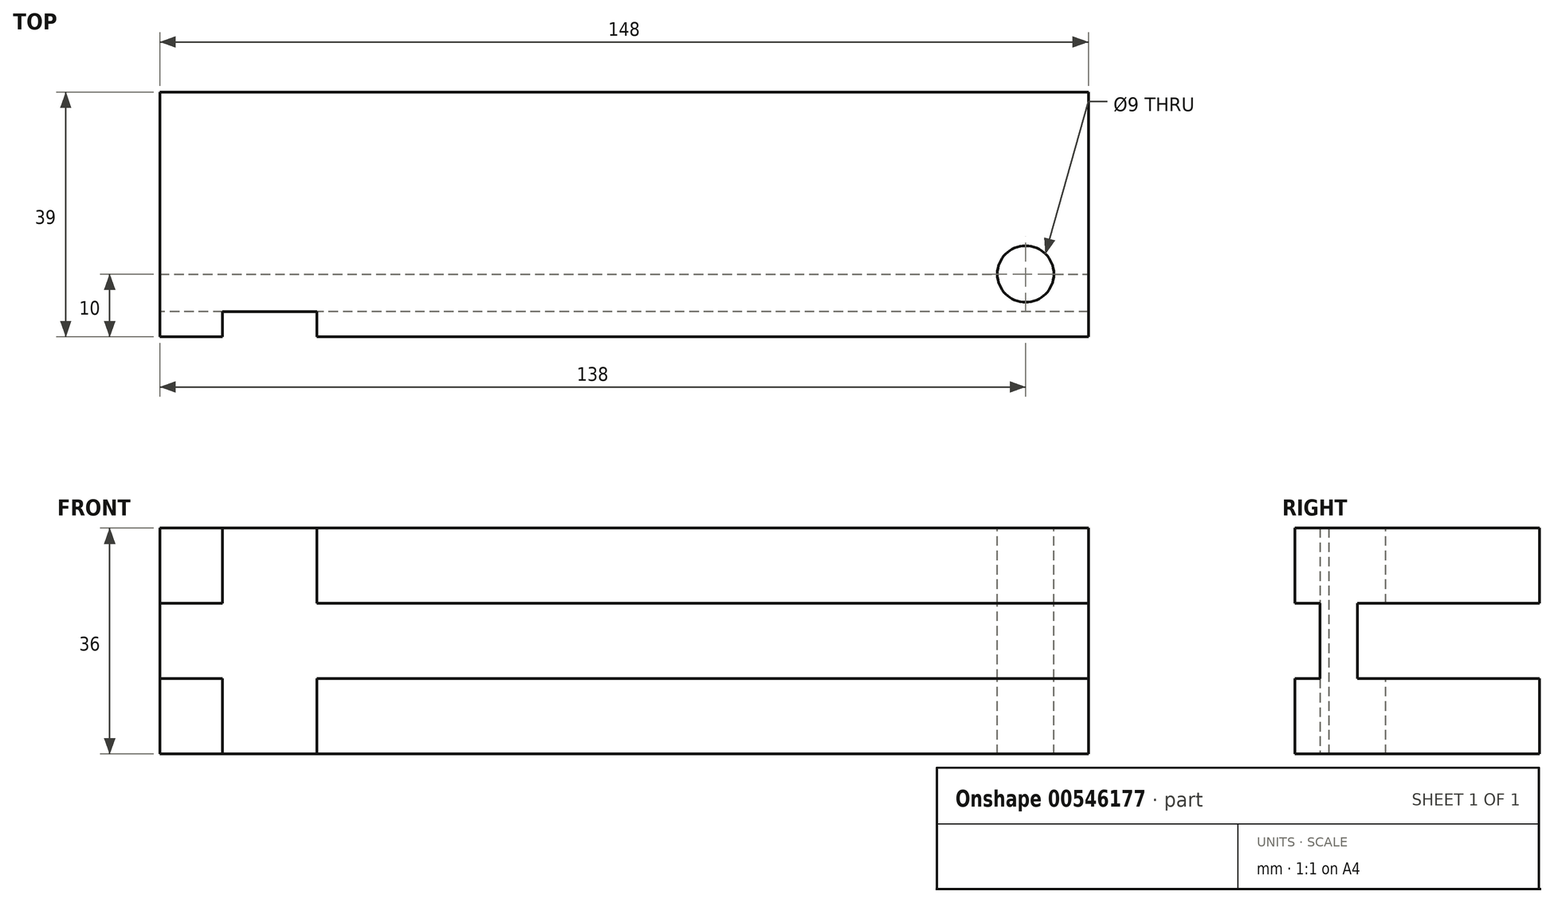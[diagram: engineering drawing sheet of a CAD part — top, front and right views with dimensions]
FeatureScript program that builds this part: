
annotation { "Feature Type Name" : "Feature", "Feature Type Description" : "" }
export const myFeature = defineFeature(function(context is Context, id is Id, definition is map)
    precondition{}
    {
        {
            var Q0;
            Q0=qCreatedBy(makeId("Front.planeOp"),FACE);
            var sketch = newSketch(context, id + "F0", { "sketchPlane" : qUnion([Q0])});
            skLineSegment(sketch, "E0.bottom", {"start": v(-74, 18) * mm, "end": v(74, 18) * mm});
            skLineSegment(sketch, "E0.top", {"start": v(-74, -18) * mm, "end": v(74, -18) * mm});
            skLineSegment(sketch, "E0.left", {"start": v(-74, 18) * mm, "end": v(-74, -18) * mm});
            skLineSegment(sketch, "E0.right", {"start": v(74, 18) * mm, "end": v(74, -18) * mm});
            skPoint(sketch, "E0.middle", {"position": v(0, 0) * mm});
            skLineSegment(sketch, "E1.bottom", {"start": v(-74, 6) * mm, "end": v(74, 6) * mm});
            skLineSegment(sketch, "E1.top", {"start": v(-74, -6) * mm, "end": v(74, -6) * mm});
            skLineSegment(sketch, "E1.left", {"start": v(-74, 6) * mm, "end": v(-74, -6) * mm});
            skLineSegment(sketch, "E1.right", {"start": v(74, 6) * mm, "end": v(74, -6) * mm});
            skSolve(sketch);
        }
        {
            var Q0;
            Q0=makeQuery(id+"F0.imprint","IMPRINT",FACE,{"disambiguationData":[TD([[makeQuery(id+"F0.imprint","IMPRINT",EDGE,{"derivedFrom":sQuery(id+"F0.wireOp",EDGE,"E0.bottom")}),-1.0]])]});
            var Q1;
            {var subQ0=sQuery(id+"F0.wireOp",EDGE,"E0.top");Q1=makeQuery(id+"F0.imprint","IMPRINT",FACE,{"disambiguationData":[TD([[makeQuery(id+"F0.imprint","IMPRINT",EDGE,{"derivedFrom":subQ0}),1.0]])]});}
            var Q2;
            Q2=makeQuery(id+"F0.imprint","IMPRINT",FACE,{"disambiguationData":[TD([[makeQuery(id+"F0.imprint","IMPRINT",EDGE,{"derivedFrom":sQuery(id+"F0.wireOp",EDGE,"E1.bottom")}),-1.0]])]});
            extrude(context, id + "F1", {"entities" : qUnion([Q0, Q1, Q2]), "depth" : 39 * mm, "offsetDistance" : 25 * mm});
        }
        {
            var Q0;
            Q0=makeQuery(id+"F0.imprint","IMPRINT",FACE,{"disambiguationData":[TD([[makeQuery(id+"F0.imprint","IMPRINT",EDGE,{"derivedFrom":sQuery(id+"F0.wireOp",EDGE,"E1.bottom")}),-1.0]])]});
            extrude(context, id + "F2", {"entities" : qUnion([Q0]), "operationType" : NewBodyOperationType.REMOVE, "depth" : 29 * mm, "offsetDistance" : 25 * mm});
        }
        {
            var Q0;
            Q0=makeQuery(id+"F1.opExtrude","CAP_FACE",FACE,{"disambiguationData":[OSD([sQuery(id+"F0.wireOp",EDGE,"E0.bottom"),sQuery(id+"F0.wireOp",EDGE,"E0.top"),sQuery(id+"F0.wireOp",EDGE,"E0.left"),sQuery(id+"F0.wireOp",EDGE,"E0.right"),sQuery(id+"F0.wireOp",EDGE,"E1.left"),sQuery(id+"F0.wireOp",EDGE,"E1.right")])],"isStart":false});
            var sketch = newSketch(context, id + "F3", { "sketchPlane" : qUnion([Q0])});
            skLineSegment(sketch, "E2.bottom", {"start": v(74, -6) * mm, "end": v(-74, -6) * mm});
            skLineSegment(sketch, "E2.top", {"start": v(74, 6) * mm, "end": v(-74, 6) * mm});
            skLineSegment(sketch, "E2.left", {"start": v(74, -6) * mm, "end": v(74, 6) * mm});
            skLineSegment(sketch, "E2.right", {"start": v(-74, -6) * mm, "end": v(-74, 6) * mm});
            skPoint(sketch, "E2.middle", {"position": v(0, 0) * mm});
            skLineSegment(sketch, "E3.bottom", {"start": v(-64, 18) * mm, "end": v(-49, 18) * mm});
            skLineSegment(sketch, "E3.top", {"start": v(-64, -18) * mm, "end": v(-49, -18) * mm});
            skLineSegment(sketch, "E3.left", {"start": v(-64, 18) * mm, "end": v(-64, -18) * mm});
            skLineSegment(sketch, "E3.right", {"start": v(-49, 18) * mm, "end": v(-49, -18) * mm});
            skSolve(sketch);
        }
        {
            var Q0;
            Q0=makeQuery(id+"F3.imprint","IMPRINT",FACE,{"disambiguationData":[TD([[makeQuery(id+"F3.imprint","IMPRINT",EDGE,{"derivedFrom":sQuery(id+"F3.wireOp",EDGE,"E2.bottom")}),-1.0]])]});
            var Q1;
            {var subQ5=sQuery(id+"F3.wireOp",EDGE,"E3.bottom");Q1=makeQuery(id+"F3.imprint","IMPRINT",FACE,{"disambiguationData":[TD([[makeQuery(id+"F3.imprint","IMPRINT",EDGE,{"derivedFrom":subQ5}),-1.0]])]});}
            var Q2;
            {var subQ5=sQuery(id+"F3.wireOp",EDGE,"E3.top");Q2=makeQuery(id+"F3.imprint","IMPRINT",FACE,{"disambiguationData":[TD([[makeQuery(id+"F3.imprint","IMPRINT",EDGE,{"derivedFrom":subQ5}),1.0]])]});}
            extrude(context, id + "F4", {"entities" : qUnion([Q0, Q1, Q2]), "operationType" : NewBodyOperationType.REMOVE, "oppositeDirection" : true, "depth" : 4 * mm, "offsetDistance" : 25 * mm});
        }
        {
            var Q0;
            Q0=makeQuery(id+"F1.opExtrude","SWEPT_FACE",FACE,{"disambiguationData":[OSD([sQuery(id+"F0.wireOp",EDGE,"E0.bottom")])]});
            var sketch = newSketch(context, id + "F5", { "sketchPlane" : qUnion([Q0])});
            skCircle(sketch, "E4", {"center": v(64, -29) * mm, "radius": 4.5 * mm});
            skSolve(sketch);
        }
        {
            var Q0;
            Q0=makeQuery(id+"F5.imprint","IMPRINT",FACE,{"disambiguationData":[TD([[makeQuery(id+"F5.imprint","IMPRINT",EDGE,{"derivedFrom":sQuery(id+"F5.wireOp",EDGE,"E4")}),1.0]])]});
            extrude(context, id + "F6", {"entities" : qUnion([Q0]), "operationType" : NewBodyOperationType.REMOVE, "oppositeDirection" : true, "depth" : 36 * mm, "offsetDistance" : 25 * mm});
        }
    });
